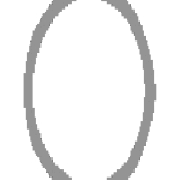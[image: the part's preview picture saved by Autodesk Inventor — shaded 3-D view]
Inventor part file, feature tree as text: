
AUTODESK INVENTOR PART (.ipt)
format: ipt  version: 2021 (Build 250183000, 183)  size: 112,128 bytes
history: native  units: in
note: dims shown in document units (in); Inventor stores cm internally (conversion verified against a paired STEP export)
features: other x4, sketch x3, plane x1
ambient origin geometry x8: Origin, YZ Plane, XZ Plane, XY Plane, X Axis, Y Axis, Z Axis, Center Point
bodies: Solid1 (feature_tree), Body (feature_tree)
feature tree (8):
  other  "Driven Length"
  other  "Frame Generator"
  other  "Start Plane"
  other  "End Plane"
  sketch  "Sketch"  dims[d2=20.6216in d4=-0.0in d5=20.6216in d6=0.12in d7=0.0in d8=90.0deg d9=20.6216in]
  sketch  "Sketch2"  dims[d0=1.0in]
  plane  "Work Plane3"
  sketch  "Sketch3"  dims[d1=0.065in]
